# Revit family: IS_ConnectSpace_E0315_BIM_FR
name_source: partatom
category: Plumbing Fixtures
revit_build: Autodesk Revit 2017 (Build: 20160225_1515(x64)
units: mm (PartAtom-declared; Revit-internal decimal feet)

## family parameters
Always vertical = No
Cut with Voids When Loaded = No
OmniClass Number = 23.45.05.14.21.11
OmniClass Title = Bath/Shower Units
Part Type = Normal
Room Calculation Point = No
Round Connector Dimension = Use Diameter
Shared = No
Work Plane-Based = No

## types (2) — shared parameters
Accessoires = www.idealspec.fr
Auteur = Ideal Standard
BOSUseNativeGeometries = 1
Bim-NomDuProjet = ISI_IdealStandard_BathroomIntegratedFurniture_ConnectSpace_E0315
Caractéristiques = CONNECT SPACE Meuble pour lavabo-plan 60 cm version droite
CodeBarre = 5017830294689
Conformité = NF
ConseilsDInstallation = 0
DateDeCréation = 2018_08_03
Description = CONNECT SPACE Meuble pour lavabo-plan 60 cm version droite
Dimensions = 590 x 396 x 513 mm
EAN code = https://5017830294689
Espace = Interne
Forme = rectangulaire
Hauteur = 513 mm
IfcExportAs = Bathroom integrated furniture
IfcExportType = IfcFurnitureType
InformationsProduit = www.idealspec.fr
Largeur = 590 mm
Longueur = 396 mm
Marque = Ideal Standard
Matériel = 0
Nom = BathroomIntegratedFurniture_ConnectSpace_E0315_IdealStandard
PoidsNet = 15,45 KG
Raccordement = Plomberie
Révision = 1
URL = www.idealspec.fr
Uniclass2015Code = Pr_40_30_78_05
Uniclass2015Title = Bathroom integrated furniture
Uniclass2015Version = Products v1.1
UnitéDeMesure = Millimètres
UnitéDeTemps = An
UnitéMonétaire = €
UrlDuFabricant = www.idealspec.fr
Version = 1
zero-valued in all types: Cost, CoûtDeRemplacement, Profondeur

## per-type parameters (varying)
| type | Couleur | Finition | Model |
| E0315KS - CONNECT SPACE MBLE SS LAV 60D BOIS BLANC | Blanc | Blanc | E0315KS |
| E0315SX - CONNECT SPACE MBLE SS LAV 60D NOYER | Noyer | Noyer | E0315SX |

## geometry (parser evidence)
native form markers: Sweep x4
no freeform markers — native parametric forms only
